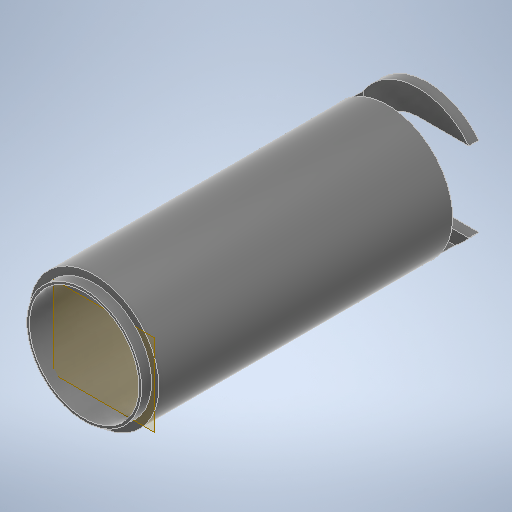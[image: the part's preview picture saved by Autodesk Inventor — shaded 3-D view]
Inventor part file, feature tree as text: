
AUTODESK INVENTOR PART (.ipt)
format: ipt  version: 2025.1 (Build 291241020, 241B)  size: 684,032 bytes
history: native  units: mm
features: extrude x9, sketch x9, plane x1, mirror x1, fillet x1
ambient origin geometry x8: Origin, YZ Plane, XZ Plane, XY Plane, X Axis, Y Axis, Z Axis, Center Point
bodies: Solid1 (feature_tree)
feature tree (21):
  extrude  "Extrusion1"  Depth=39.0mm
  plane  "Work Plane1"
  extrude  "Extrusion2"  Depth=3.0mm TaperAngle=0.0deg
  mirror  "Mirror1"
  extrude  "Extrusion5"  Depth=10.0mm TaperAngle=0.0deg
  extrude  "Extrusion6"  Depth=9.0mm
  extrude  "Extrusion7"  Depth=20.0mm
  extrude  "Extrusion8"  TaperAngle=0.0deg  [1 undecoded]
  extrude  "Extrusion9"  Depth=33.0mm
  extrude  "Extrusion10"  TaperAngle=0.0deg  [1 undecoded]
  extrude  "Extrusion12"  [1 undecoded]
  fillet  "Fillet1"  [1 undecoded]
  sketch  "Sketch1"  dims[d0=33.0mm d1=39.0mm]
  sketch  "Sketch2"  dims[d2=195.0mm d3=0.0mm d4=3.0mm d5=0.0mm]
  sketch  "Sketch5"  dims[d12=24.0mm d13=10.0mm d14=0.0mm]
  sketch  "Sketch6"  dims[d15=0.0mm d16=0.0mm d17=9.0mm]
  sketch  "Sketch7"  dims[d18=0.0mm d19=0.0mm d20=20.0mm]
  sketch  "Sketch8"  dims[d21=5.0mm d22=0.0mm d23=0.0mm d24=0.0mm]
  sketch  "Sketch9"  dims[d25=0.8mm d26=33.0mm]
  sketch  "Sketch10"  dims[d28=3.0mm d29=0.0mm d33=0.0mm d34=0.0mm]
  sketch  "Sketch12"  dims[d35=2.0mm]
note: 4 required parameter values undecoded (feature->parameter linkage not recoverable at this tier; creation-order binding heuristic only, values carry confidence <= 0.55)
